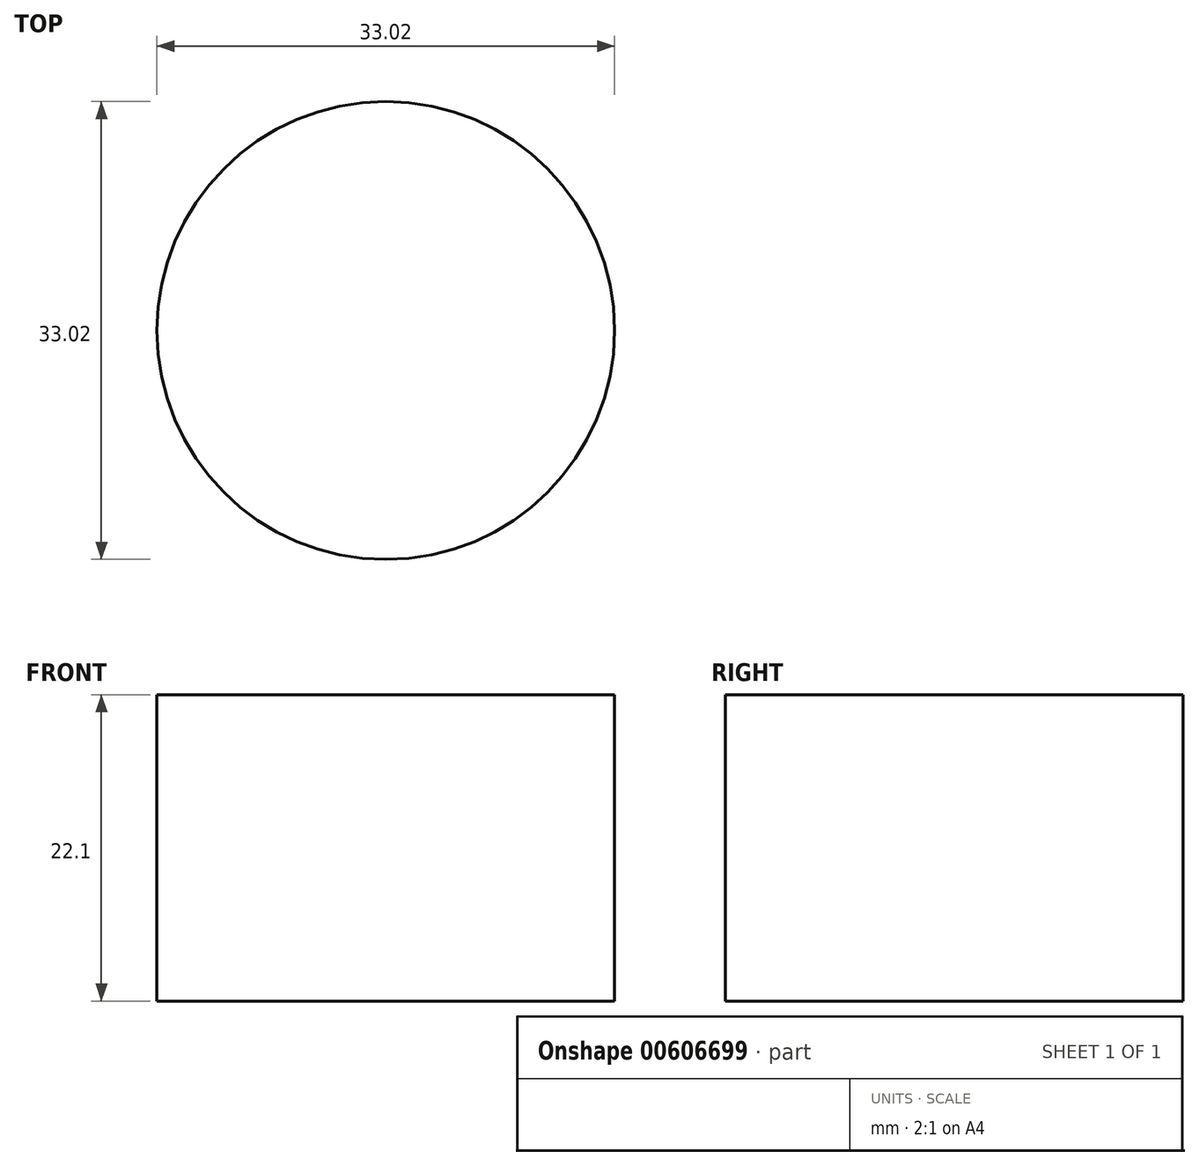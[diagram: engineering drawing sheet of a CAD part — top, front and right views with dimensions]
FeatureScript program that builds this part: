
annotation { "Feature Type Name" : "Feature", "Feature Type Description" : "" }
export const myFeature = defineFeature(function(context is Context, id is Id, definition is map)
    precondition{}
    {
        {
            var Q0;
            Q0=qCreatedBy(makeId("Top.planeOp"),FACE);
            var sketch = newSketch(context, id + "F0", { "sketchPlane" : qUnion([Q0])});
            skCircle(sketch, "E0", {"center": v(0, 0) * mm, "radius": 16.51 * mm});
            skSolve(sketch);
        }
        {
            var Q0;
            Q0 = qSketchRegion(id + "F0", true);
            extrude(context, id + "F1", {"entities" : qUnion([Q0]), "depth" : 22.1 * mm, "offsetDistance" : 25.4 * mm});
        }
    });
